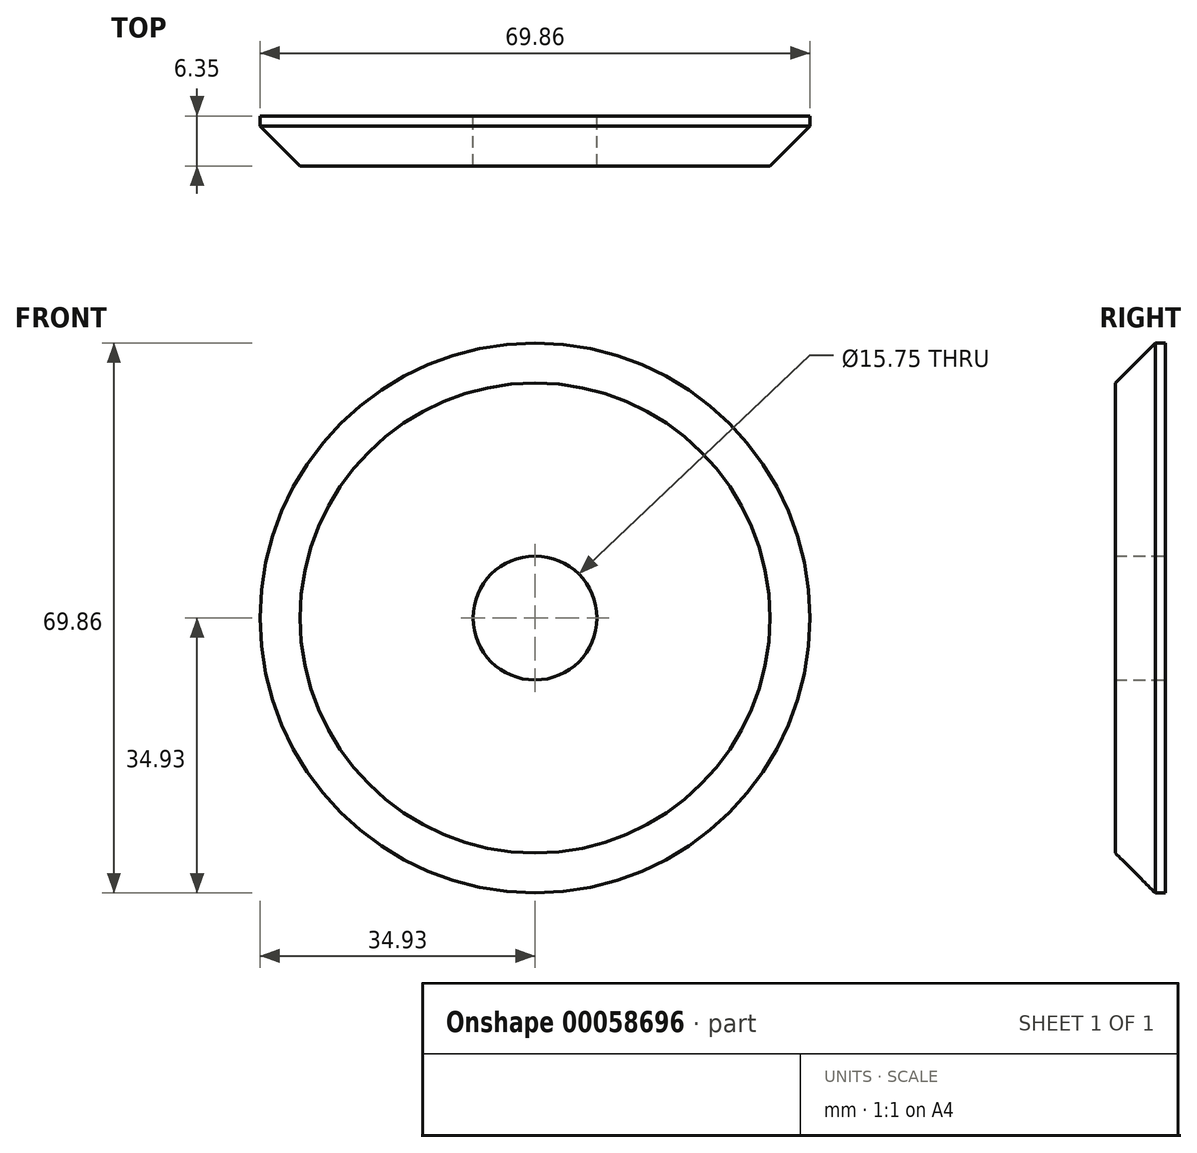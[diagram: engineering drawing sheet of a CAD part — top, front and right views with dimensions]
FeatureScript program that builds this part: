
annotation { "Feature Type Name" : "Feature", "Feature Type Description" : "" }
export const myFeature = defineFeature(function(context is Context, id is Id, definition is map)
    precondition{}
    {
        {
            var Q0;
            Q0=qCreatedBy(makeId("Front.planeOp"),FACE);
            var sketch = newSketch(context, id + "F0", { "sketchPlane" : qUnion([Q0])});
            skCircle(sketch, "E0", {"center": v(0, 0) * mm, "radius": 34.93 * mm});
            skCircle(sketch, "E1", {"center": v(0, 0) * mm, "radius": 7.87 * mm});
            skSolve(sketch);
        }
        {
            var Q0;
            Q0=makeQuery(id+"F0.imprint","IMPRINT",FACE,{"disambiguationData":[TD([[makeQuery(id+"F0.imprint","IMPRINT",EDGE,{"derivedFrom":sQuery(id+"F0.wireOp",EDGE,"E0")}),1.0]])]});
            extrude(context, id + "F1", {"entities" : qUnion([Q0]), "depth" : 6.35 * mm});
        }
        {
            var Q0;
            Q0=makeQuery(id+"F1.opExtrude","CAP_EDGE",EDGE,{"disambiguationData":[OSD([sQuery(id+"F0.wireOp",EDGE,"E0")])],"isStart":false});
            chamfer(context, id + "F2", {"entities" : qUnion([Q0]), "width" : 5.08 * mm, "tangentPropagation" : true});
        }
    });
